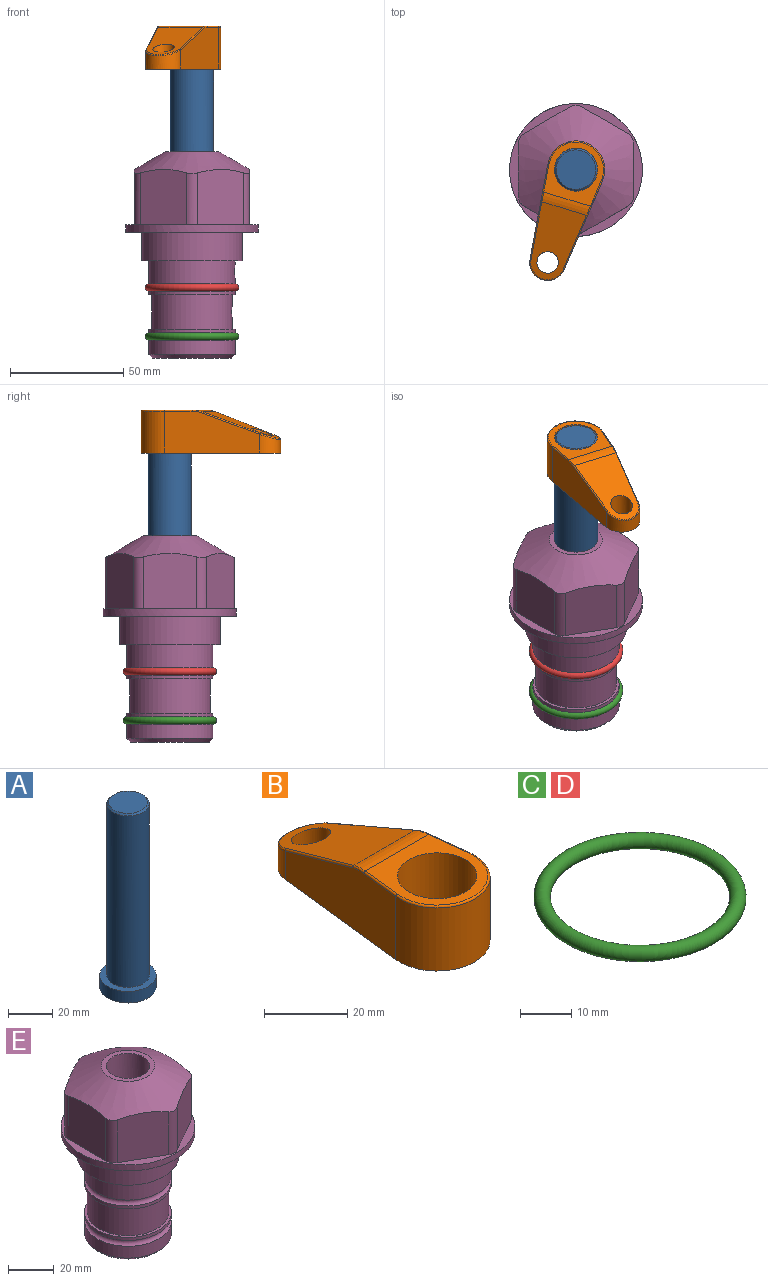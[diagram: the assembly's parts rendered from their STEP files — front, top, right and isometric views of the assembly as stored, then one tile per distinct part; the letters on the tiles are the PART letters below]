
ASSEMBLY  parts=5 mates=3
PART A: 6 faces, bbox 25.4x25.4x101.6 mm
  f0: plane 17.46x17.46mm, normal (0,0,1), area 239.5mm2, adj f5
  f1: plane 25.4x25.4mm, normal (0,0,-1), area 506.7mm2, adj f2
  f2: cylinder r=12.7mm len=25.4mm, axis (0,0,1), area 506.7mm2, adj f1,f3
  f3: plane 25.4x25.4mm, normal (0,0,1), area 221.7mm2, adj f2,f4
  f4: cylinder r=9.53mm len=94.46mm, axis (0,0,1), area 5653mm2, adj f3,f5
  f5: cone r=8.73mm half-angle=45deg, axis (0,0,-1), area 64.4mm2, adj f0,f4
PART B: 44 faces, bbox 27.5x64.5x19.1 mm
  f0: plane 2.3x0.95mm, normal (0,0,-1), area 1mm2, adj f25,f30,f34
  f1: plane 63.5x25.4mm, normal (0,0,-1), area 561.7mm2, adj f2,f3,f4,f5,f6,f7,f19,f20
  f2: cylinder r=12.7mm len=25.4mm, axis (0,0,-1), area 792.2mm2, adj f1,f3,f5,f13
  f3: plane 42.33x18.54mm, normal (0.99,0.11,0), area 647mm2, adj f1,f2,f4,f11,f12,f14
  f4: cylinder r=7.94mm len=15.78mm, axis (0,0,-1), area 158.6mm2, adj f1,f3,f5,f16
  f5: plane 42.33x18.54mm, normal (-0.99,0.11,0), area 647mm2, adj f1,f2,f4,f15,f17,f18
  f6: cylinder r=9.53mm len=19.05mm, axis (0,0,-1), area 1140.1mm2, adj f1,f8
  f7: cylinder r=4.76mm len=10.98mm, axis (0,0,-1), area 276.1mm2, adj f1,f9
  f8: plane 25.83x24.38mm, normal (0,0,1), area 262.2mm2, adj f6,f10,f11,f13,f15
  f9: plane 32.49x20.55mm, normal (0,0.34,0.94), area 489.9mm2, adj f7,f10,f14,f16,f18
  f10: cylinder r=12.7mm len=21.49mm, axis (-1,0,0), area 93.2mm2, adj f8,f9,f12,f17
  f11: cylinder r=0.51mm len=12.34mm, axis (0.11,-0.99,0), area 9.9mm2, adj f3,f8,f12,f13
  f12: bspline ~7.62x1.64mm, area 3.5mm2, adj f3,f10,f11,f14
  f13: torus R=12.19mm, axis (0,0,1), area 33.6mm2, adj f2,f8,f11,f15
  f14: cylinder r=0.51mm len=26.01mm, axis (0.1,-0.93,0.34), area 21.6mm2, adj f3,f9,f12,f16
  f15: cylinder r=0.51mm len=12.34mm, axis (0.11,0.99,0), area 9.9mm2, adj f5,f8,f13,f17
  f16: bspline ~15.78x7.05mm, area 15.7mm2, adj f4,f9,f14,f18
  f17: bspline ~7.62x1.64mm, area 3.5mm2, adj f5,f10,f15,f18
  f18: cylinder r=0.51mm len=26.01mm, axis (0.1,0.93,-0.34), area 21.6mm2, adj f5,f9,f16,f17
  f19: plane 21.6x14.29mm, normal (-0.99,-0.11,0), area 242.6mm2, adj f1,f26,f28,f34,f36,f38
  f20: plane 21.6x14.29mm, normal (0.99,-0.11,0), area 242.6mm2, adj f1,f27,f29,f37,f39,f41
  f21: cylinder r=12.7mm len=14.29mm, axis (0,0,-1), area 173.2mm2, adj f1,f26,f27,f30,f31,f33
  f22: cylinder r=7.94mm len=7.63mm, axis (0,0,-1), area 53.8mm2, adj f1,f28,f29,f42
  f23: plane 2.3x0.95mm, normal (0,0,-1), area 1mm2, adj f25,f33,f37
  f24: plane 17.94x12.32mm, normal (0,-0.34,-0.94), area 191.2mm2, adj f25,f38,f41,f42
  f25: cylinder r=9.53mm len=12.93mm, axis (-1,0,0), area 37.5mm2, adj f0,f23,f24,f31,f36,f39
  f26: cylinder r=1.59mm len=14.29mm, axis (0,0,-1), area 49mm2, adj f1,f19,f21,f32
  f27: cylinder r=1.59mm len=14.29mm, axis (0,0,-1), area 49mm2, adj f1,f20,f21,f35
  f28: cylinder r=1.59mm len=7.28mm, axis (0,0,-1), area 22.1mm2, adj f1,f19,f22,f40
  f29: cylinder r=1.59mm len=7.28mm, axis (0,0,-1), area 22.1mm2, adj f1,f20,f22,f43
  f30: torus R=14.29mm, axis (0,0,1), area 5.8mm2, adj f0,f21,f31,f32
  f31: bspline ~11.06x2.73mm, area 20.8mm2, adj f21,f25,f30,f33
  f32: sphere r=1.59mm, area 5.4mm2, adj f26,f30,f34
  f33: torus R=14.29mm, axis (0,0,1), area 5.8mm2, adj f21,f23,f31,f35
  f34: cylinder r=1.59mm len=1.68mm, axis (-0.11,0.99,0), area 2.4mm2, adj f0,f19,f32,f36
  f35: sphere r=1.59mm, area 5.4mm2, adj f27,f33,f37
  f36: bspline ~5.82x2.33mm, area 7.7mm2, adj f19,f25,f34,f38
  f37: cylinder r=1.59mm len=1.68mm, axis (0.11,0.99,0), area 2.4mm2, adj f20,f23,f35,f39
  f38: cylinder r=1.59mm len=18.33mm, axis (0.1,-0.93,0.34), area 46.7mm2, adj f19,f24,f36,f40
  f39: bspline ~5.82x2.33mm, area 7.7mm2, adj f20,f25,f37,f41
  f40: sphere r=1.59mm, area 3.6mm2, adj f28,f38,f42
  f41: cylinder r=1.59mm len=18.33mm, axis (0.1,0.93,-0.34), area 46.7mm2, adj f20,f24,f39,f43
  f42: bspline ~8.31x1.84mm, area 15.3mm2, adj f22,f24,f40,f43
  f43: sphere r=1.59mm, area 3.6mm2, adj f29,f41,f42
PART C: 1 faces, bbox 44.7x44.7x3.2 mm
  f0: torus R=19.05mm, axis (0,0,1), area 1193.9mm2
PART D: same geometry as C
PART E: 36 faces, bbox 58.7x58.7x91.2 mm
  f0: cylinder r=17.78mm len=35.56mm, axis (0,0,1), area 1670.8mm2, adj f23,f24,f31
  f1: cylinder r=19.05mm len=38.1mm, axis (0,0,1), area 1191.9mm2, adj f26,f27,f30
  f2: plane 58.66x58.66mm, normal (0,0,-1), area 1150.6mm2, adj f3,f28
  f3: cylinder r=29.33mm len=58.66mm, axis (0,0,-1), area 585.1mm2, adj f2,f4
  f4: plane 58.66x58.66mm, normal (0,0,1), area 475.9mm2, adj f3,f5,f6,f7,f8,f9,f10,f11
  f5: plane 24.5x20.32mm, normal (-0.5,0.87,0), area 562.8mm2, adj f4,f15,f16,f17
  f6: plane 24.5x20.32mm, normal (0.5,0.87,0), area 562.8mm2, adj f4,f14,f15,f17
  f7: plane 24.5x23.48mm, normal (1,0,0), area 562.8mm2, adj f4,f13,f14,f17
  f8: plane 24.5x20.32mm, normal (0.5,-0.87,0), area 562.8mm2, adj f4,f12,f13,f17
  f9: plane 24.5x20.32mm, normal (-0.5,-0.87,0), area 562.8mm2, adj f4,f11,f12,f17
  f10: plane 24.5x23.48mm, normal (-1,0,0), area 562.8mm2, adj f4,f11,f16,f17
  f11: cylinder r=5.08mm len=23.01mm, axis (0,0,-1), area 121.2mm2, adj f4,f9,f10,f17
  f12: cylinder r=5.08mm len=23.01mm, axis (0,0,-1), area 121.2mm2, adj f4,f8,f9,f17
  f13: cylinder r=5.08mm len=23.01mm, axis (0,0,-1), area 121.2mm2, adj f4,f7,f8,f17
  f14: cylinder r=5.08mm len=23.01mm, axis (0,0,-1), area 121.2mm2, adj f4,f6,f7,f17
  f15: cylinder r=5.08mm len=23.01mm, axis (0,0,-1), area 121.2mm2, adj f4,f5,f6,f17
  f16: cylinder r=5.08mm len=23.01mm, axis (0,0,-1), area 121.2mm2, adj f4,f5,f10,f17
  f17: cone r=11.73mm half-angle=60deg, axis (0,0,-1), area 2071.8mm2, adj f5,f6,f7,f8,f9,f10,f11,f12
  f18: plane 23.46x23.46mm, normal (0,0,1), area 147.4mm2, adj f17,f35
  f19: plane 34.93x34.93mm, normal (0,0,-1), area 958mm2, adj f29
  f20: cylinder r=19.05mm len=38.1mm, axis (0,0,1), area 760.1mm2, adj f21,f29
  f21: torus R=19.05mm, axis (0,0,1), area 565.3mm2, adj f20,f22
  f22: cylinder r=19.05mm len=38.1mm, axis (0,0,1), area 190mm2, adj f21,f23
  f23: plane 38.1x38.1mm, normal (0,0,1), area 146.9mm2, adj f0,f22
  f24: plane 38.1x38.1mm, normal (0,0,-1), area 146.9mm2, adj f0,f25
  f25: cylinder r=19.05mm len=38.1mm, axis (0,0,1), area 190mm2, adj f24,f26
  f26: torus R=19.05mm, axis (0,0,1), area 565.3mm2, adj f1,f25
  f27: plane 44.45x44.45mm, normal (0,0,-1), area 411.7mm2, adj f1,f28
  f28: cylinder r=22.23mm len=44.45mm, axis (0,0,1), area 1773.5mm2, adj f2,f27
  f29: cone r=19.05mm half-angle=45deg, axis (0,0,1), area 257.5mm2, adj f19,f20
  f30: cylinder r=3.17mm len=6.75mm, axis (-1,0,0), area 128mm2, adj f1,f33
  f31: cylinder r=3.17mm len=6.35mm, axis (-1,0,0), area 102.5mm2, adj f0,f33
  f32: plane 25.4x25.4mm, normal (0,0,1), area 506.7mm2, adj f33
  f33: cylinder r=12.7mm len=66.42mm, axis (0,0,-1), area 5236.2mm2, adj f30,f31,f32,f34
  f34: cone r=9.53mm half-angle=30deg, axis (0,0,-1), area 443.4mm2, adj f33,f35
  f35: cylinder r=9.53mm len=19.05mm, axis (0,0,-1), area 849mm2, adj f18,f34
PLACE A rot(axis=(0,0,-1),106.9deg) t=(0,0,17.38)mm
PLACE B rot(axis=(0,0,1),163.1deg) t=(0,0,71.99)mm
PLACE C t=(0,0,-21.59)mm
PLACE D at identity
PLACE E at identity fixed
MATE fastened C.f0 <-> E.f0  axis (0,0,1) through (0,0,-46.1)mm
MATE cylindrical A.f2 <-> E.f0  axis (0,0,1) through (0,0,43.02)mm
MATE fastened B.f2 <-> A.f2  axis (0,0,1) through (0,0,91.04)mm
